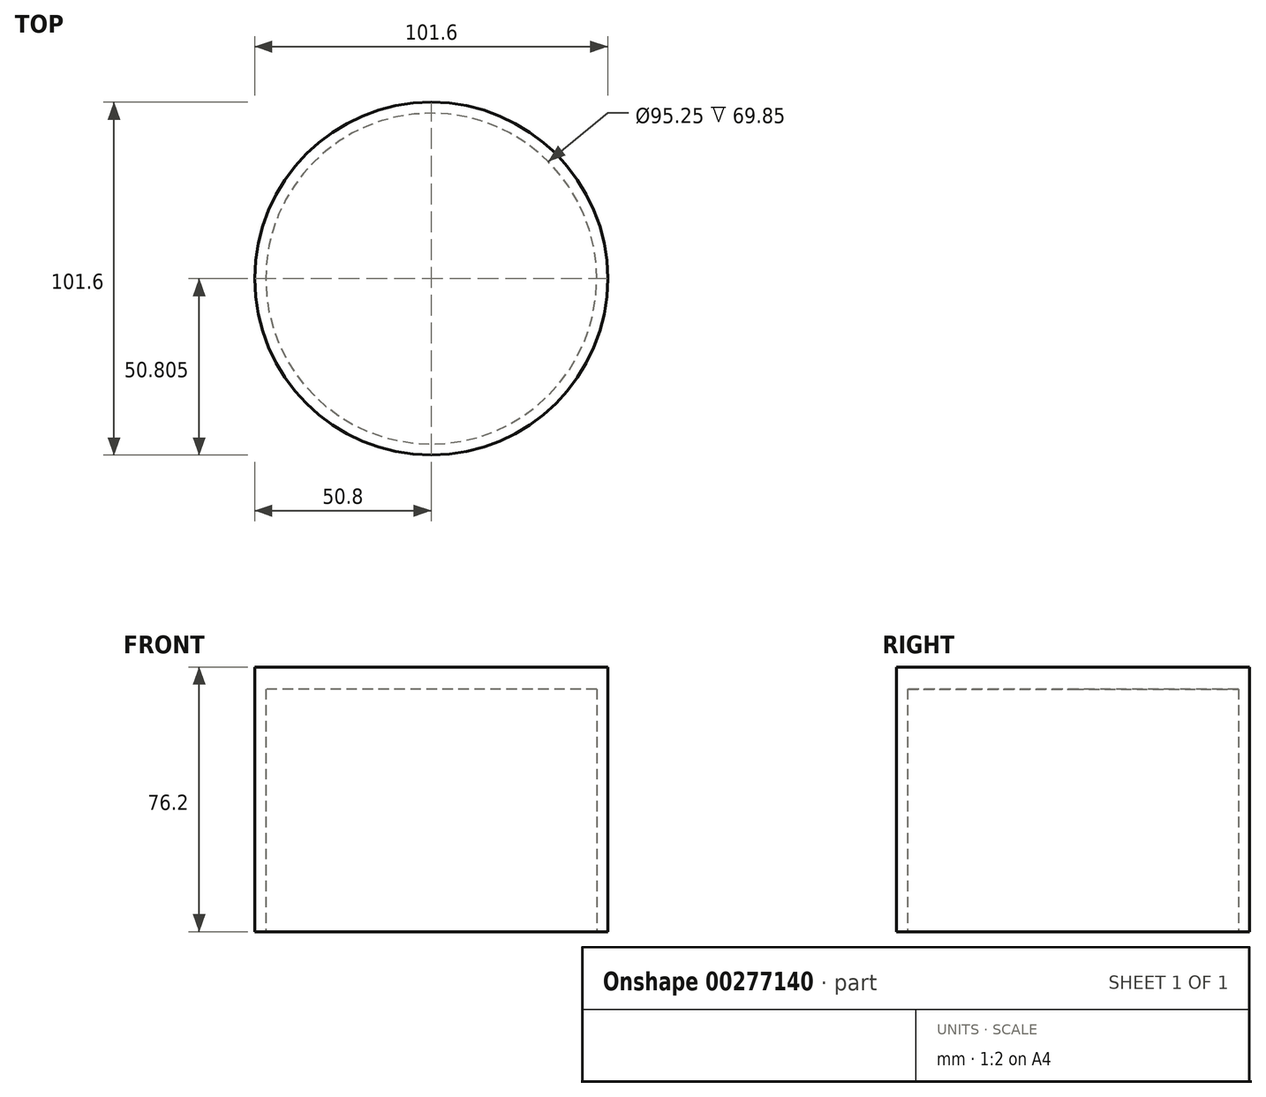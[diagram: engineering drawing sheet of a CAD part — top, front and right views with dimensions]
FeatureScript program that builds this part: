
annotation { "Feature Type Name" : "Feature", "Feature Type Description" : "" }
export const myFeature = defineFeature(function(context is Context, id is Id, definition is map)
    precondition{}
    {
        {
            var Q0;
            Q0=qCreatedBy(makeId("Top.planeOp"),FACE);
            var sketch = newSketch(context, id + "F0", { "sketchPlane" : qUnion([Q0])});
            skCircle(sketch, "E0", {"center": v(-47.01, 38.71) * mm, "radius": 50.8 * mm});
            skCircle(sketch, "E1", {"center": v(-47.01, 38.71) * mm, "radius": 47.63 * mm});
            skSolve(sketch);
        }
        {
            var Q0;
            Q0=makeQuery(id+"F0.imprint","IMPRINT",FACE,{"disambiguationData":[TD([[makeQuery(id+"F0.imprint","IMPRINT",EDGE,{"derivedFrom":sQuery(id+"F0.wireOp",EDGE,"E1")}),1.0]])]});
            var Q1;
            Q1=makeQuery(id+"F0.imprint","IMPRINT",FACE,{"disambiguationData":[TD([[makeQuery(id+"F0.imprint","IMPRINT",EDGE,{"derivedFrom":sQuery(id+"F0.wireOp",EDGE,"E0")}),1.0]])]});
            extrude(context, id + "F1", {"entities" : qUnion([Q0, Q1]), "depth" : 76.2 * mm});
        }
        {
            var Q0;
            Q0=makeQuery(id+"F0.imprint","IMPRINT",FACE,{"disambiguationData":[TD([[makeQuery(id+"F0.imprint","IMPRINT",EDGE,{"derivedFrom":sQuery(id+"F0.wireOp",EDGE,"E1")}),1.0]])]});
            extrude(context, id + "F2", {"entities" : qUnion([Q0]), "operationType" : NewBodyOperationType.REMOVE, "depth" : 69.85 * mm});
        }
    });
